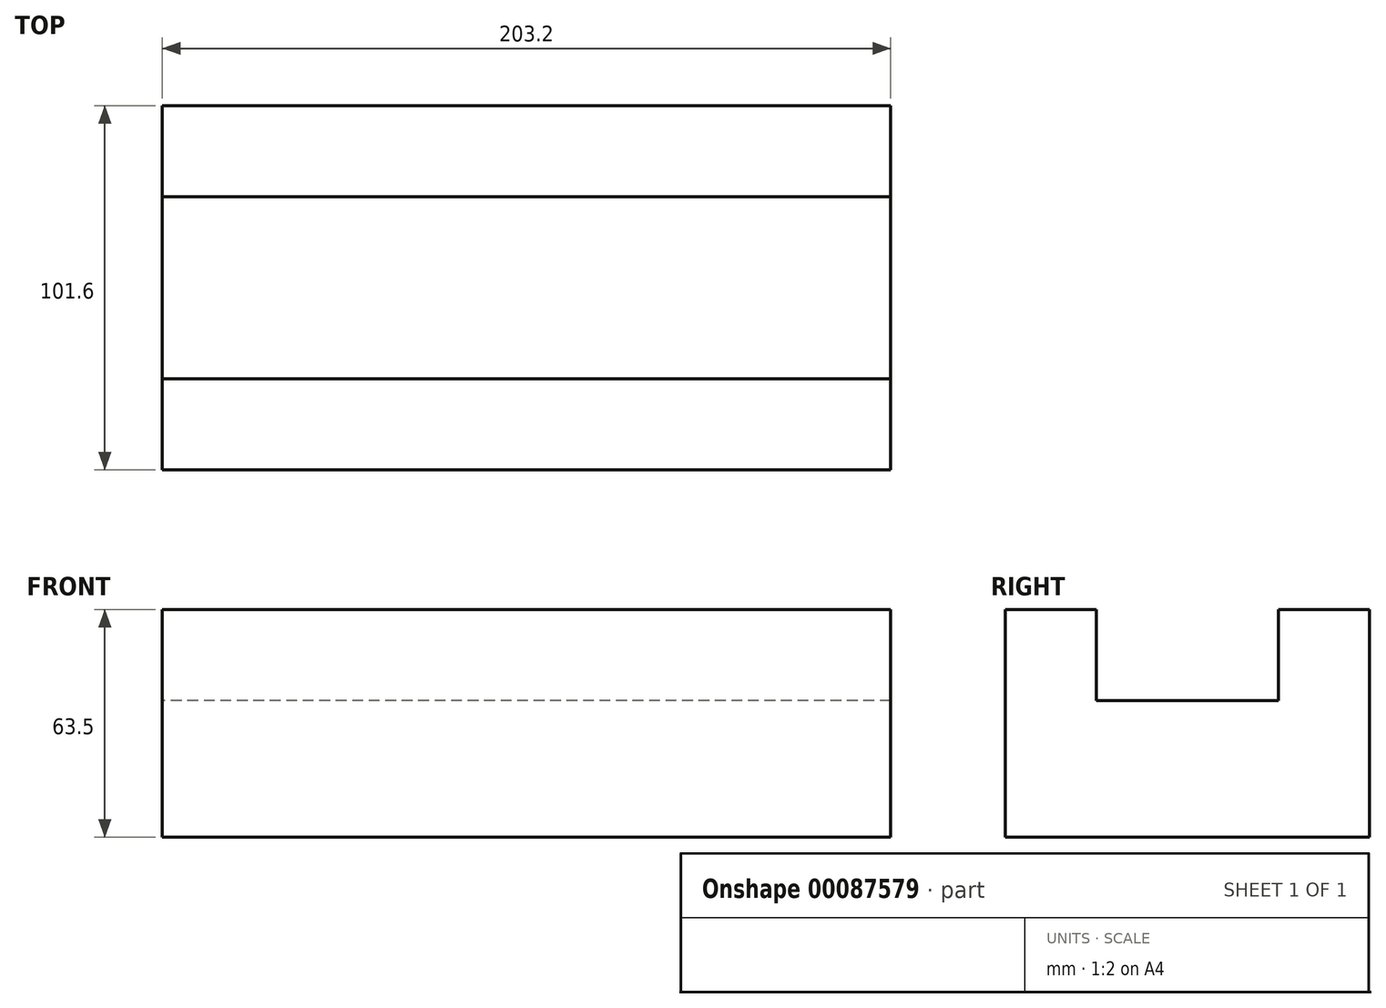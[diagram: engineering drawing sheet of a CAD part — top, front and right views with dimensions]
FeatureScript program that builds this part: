
annotation { "Feature Type Name" : "Feature", "Feature Type Description" : "" }
export const myFeature = defineFeature(function(context is Context, id is Id, definition is map)
    precondition{}
    {
        {
            var Q0;
            Q0=qCreatedBy(makeId("Right.planeOp"),FACE);
            var sketch = newSketch(context, id + "F0", { "sketchPlane" : qUnion([Q0])});
            skLineSegment(sketch, "E0.bottom", {"start": v(0, 0) * mm, "end": v(101.6, 0) * mm});
            skLineSegment(sketch, "E0.top", {"start": v(0, 38.1) * mm, "end": v(101.6, 38.1) * mm});
            skLineSegment(sketch, "E0.left", {"start": v(0, 0) * mm, "end": v(0, 38.1) * mm});
            skLineSegment(sketch, "E0.right", {"start": v(101.6, 0) * mm, "end": v(101.6, 38.1) * mm});
            skLineSegment(sketch, "E1.bottom", {"start": v(0, 38.1) * mm, "end": v(25.4, 38.1) * mm});
            skLineSegment(sketch, "E1.top", {"start": v(0, 63.5) * mm, "end": v(25.4, 63.5) * mm});
            skLineSegment(sketch, "E1.left", {"start": v(0, 38.1) * mm, "end": v(0, 63.5) * mm});
            skLineSegment(sketch, "E1.right", {"start": v(25.4, 38.1) * mm, "end": v(25.4, 63.5) * mm});
            skLineSegment(sketch, "E2.bottom", {"start": v(101.6, 38.1) * mm, "end": v(76.2, 38.1) * mm});
            skLineSegment(sketch, "E2.top", {"start": v(101.6, 63.5) * mm, "end": v(76.2, 63.5) * mm});
            skLineSegment(sketch, "E2.left", {"start": v(101.6, 38.1) * mm, "end": v(101.6, 63.5) * mm});
            skLineSegment(sketch, "E2.right", {"start": v(76.2, 38.1) * mm, "end": v(76.2, 63.5) * mm});
            skLineSegment(sketch, "E3", {"start": v(25.4, 38.1) * mm, "end": v(0, 63.5) * mm});
            skLineSegment(sketch, "E4", {"start": v(101.6, 63.5) * mm, "end": v(76.2, 38.1) * mm});
            skLineSegment(sketch, "E5", {"start": v(76.2, 63.5) * mm, "end": v(25.4, 63.5) * mm});
            skSolve(sketch);
        }
        {
            var Q0;
            Q0=makeQuery(id+"F0.imprint","IMPRINT",FACE,{"disambiguationData":[TD([[makeQuery(id+"F0.imprint","IMPRINT",EDGE,{"derivedFrom":sQuery(id+"F0.wireOp",EDGE,"E1.top")}),-1.0]])]});
            var Q1;
            Q1=makeQuery(id+"F0.imprint","IMPRINT",FACE,{"disambiguationData":[TD([[makeQuery(id+"F0.imprint","IMPRINT",EDGE,{"derivedFrom":sQuery(id+"F0.wireOp",EDGE,"E0.top")}),1.0]])]});
            var Q2;
            Q2=makeQuery(id+"F0.imprint","IMPRINT",FACE,{"disambiguationData":[TD([[makeQuery(id+"F0.imprint","IMPRINT",EDGE,{"derivedFrom":sQuery(id+"F0.wireOp",EDGE,"E2.top")}),1.0]])]});
            var Q3;
            Q3=makeQuery(id+"F0.imprint","IMPRINT",FACE,{"disambiguationData":[TD([[makeQuery(id+"F0.imprint","IMPRINT",EDGE,{"derivedFrom":sQuery(id+"F0.wireOp",EDGE,"E0.bottom")}),1.0]])]});
            extrude(context, id + "F1", {"entities" : qUnion([Q0, Q1, Q2, Q3]), "depth" : 203.2 * mm});
        }
    });
